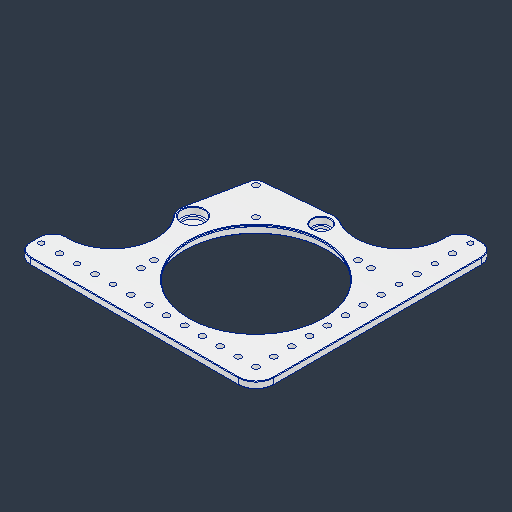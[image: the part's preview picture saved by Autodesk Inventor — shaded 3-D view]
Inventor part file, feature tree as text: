
AUTODESK INVENTOR PART (.ipt)
format: ipt  version: 2024.3 (Build 283343000, 343)  size: 359,424 bytes
history: native  units: in
note: dims shown in document units (in); Inventor stores cm internally (conversion verified against a paired STEP export)
features: chamfer x1
ambient origin geometry x8: Origin, YZ Plane, XZ Plane, XY Plane, X Axis, Y Axis, Z Axis, Center Point
bodies: Solid15 (feature_tree)
feature tree (1):
  chamfer  "Chamfer2"  [1 undecoded]
note: 1 required parameter value undecoded (feature->parameter linkage not recoverable at this tier; creation-order binding heuristic only, values carry confidence <= 0.55)
